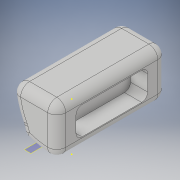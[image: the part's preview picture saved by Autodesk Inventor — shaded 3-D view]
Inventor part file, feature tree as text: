
AUTODESK INVENTOR PART (.ipt)
format: ipt  version: 2018 (Build 220112000, 112)  size: 198,656 bytes
history: native  units: in
note: dims shown in document units (in); Inventor stores cm internally (conversion verified against a paired STEP export)
features: sketch x4, fillet x4, extrude x2, plane x1
ambient origin geometry x8: Origin, YZ Plane, XZ Plane, XY Plane, X Axis, Y Axis, Z Axis, Center Point
bodies: Solid1 (feature_tree)
feature tree (11):
  sketch  "Sketch1"  dims[d8=1.53in d9=2.3in]
  extrude  "Extrusion1"  Depth=2.3in
  plane  "Work Plane1"
  extrude  "Extrusion2"  Depth=3.17in TaperAngle=0.0deg
  fillet  "Fillet1"  [1 undecoded]
  fillet  "Fillet2"  Radius=2.39in
  fillet  "Fillet3"  Radius=0.93in
  fillet  "Fillet4"  Radius=0.57in
  sketch  "Sketch4"  dims[d21=0.3in d22=0.3in d23=0.3in]
  sketch  "Sketch2"  dims[d10=2.356in d11=3.17in d12=0.5in d13=0.0in d14=0.0in d15=0.0in d16=2.39in d17=0.93in d18=0.57in d19=0.0in]
  sketch  "Sketch3"  dims[d20=0.2in]
note: 1 required parameter value undecoded (feature->parameter linkage not recoverable at this tier; creation-order binding heuristic only, values carry confidence <= 0.55)
